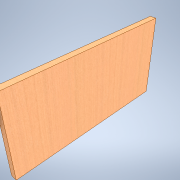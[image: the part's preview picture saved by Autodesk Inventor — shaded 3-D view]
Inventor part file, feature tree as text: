
AUTODESK INVENTOR PART (.ipt)
format: ipt  version: 2021 (Build 250183000, 183)  size: 110,592 bytes
history: native  units: mm
features: extrude x1, sketch x1
ambient origin geometry x8: Origin, YZ Plane, XZ Plane, XY Plane, X Axis, Y Axis, Z Axis, Center Point
bodies: Solid1 (feature_tree)
feature tree (2):
  extrude  "Extrusion1"  [1 undecoded]
  sketch  "Sketch1"  dims[d3=0.0mm]
note: 1 required parameter value undecoded (feature->parameter linkage not recoverable at this tier; creation-order binding heuristic only, values carry confidence <= 0.55)
